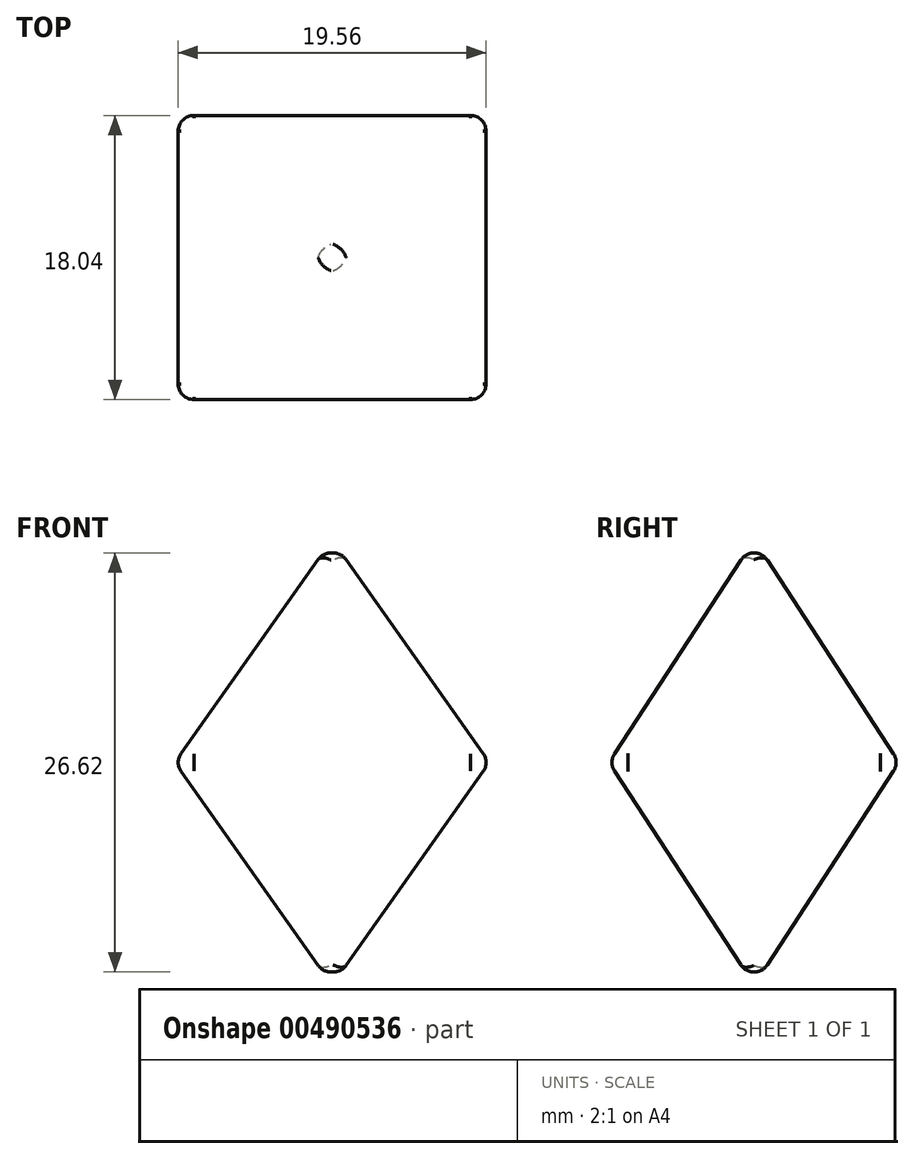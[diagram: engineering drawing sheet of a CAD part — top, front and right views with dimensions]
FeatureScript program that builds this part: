
annotation { "Feature Type Name" : "Feature", "Feature Type Description" : "" }
export const myFeature = defineFeature(function(context is Context, id is Id, definition is map)
    precondition{}
    {
        {
            var Q0;
            Q0=qCreatedBy(makeId("Top.planeOp"),FACE);
            var sketch = newSketch(context, id + "F0", { "sketchPlane" : qUnion([Q0])});
            skLineSegment(sketch, "E0.bottom", {"start": v(10, -9.22) * mm, "end": v(-10, -9.22) * mm});
            skLineSegment(sketch, "E0.top", {"start": v(10, 9.22) * mm, "end": v(-10, 9.22) * mm});
            skLineSegment(sketch, "E0.left", {"start": v(10, -9.22) * mm, "end": v(10, 9.22) * mm});
            skLineSegment(sketch, "E0.right", {"start": v(-10, -9.22) * mm, "end": v(-10, 9.22) * mm});
            skPoint(sketch, "E0.middle", {"position": v(0, 0) * mm});
            skPoint(sketch, "E1", {"position": v(-10, -9.22) * mm});
            skPoint(sketch, "E2", {"position": v(10, -9.22) * mm});
            skPoint(sketch, "E3", {"position": v(-10, 9.22) * mm});
            skPoint(sketch, "E4", {"position": v(10, 8.54) * mm});
            skSolve(sketch);
        }
        {
            var Q0;
            Q0=qCreatedBy(makeId("Front.planeOp"),FACE);
            var sketch = newSketch(context, id + "F1", { "sketchPlane" : qUnion([Q0])});
            skLineSegment(sketch, "E5", {"start": v(0, 0) * mm, "end": v(0, 14.14) * mm});
            skPoint(sketch, "E6", {"position": v(0, 14.14) * mm});
            skLineSegment(sketch, "E7.MirrorCS", {"start": v(0, 0) * mm, "end": v(0, -14.14) * mm});
            skSolve(sketch);
        }
        {
            var Q0;
            Q0=makeQuery(id+"F0.imprint","IMPRINT",FACE,{"disambiguationData":[TD([[makeQuery(id+"F0.imprint","IMPRINT",EDGE,{"derivedFrom":sQuery(id+"F0.wireOp",EDGE,"E0.bottom")}),-1.0]])]});
            var Q1;
            Q1=sQuery(id+"F1.wireOp",VERTEX,"E6");
            loft(context, id + "F2", {"sheetProfilesArray" : [{ "sheetProfileEntities" : qUnion([Q0]) }, { "sheetProfileEntities" : qUnion([Q1]) }]});
        }
        {
            var Q1;
            Q1=makeQuery(id+"F2.opLoft","CAP_FACE",FACE,{"disambiguationData":[OSD([makeQuery(id+"F0.imprint","IMPRINT",FACE,{"disambiguationData":[TD([[makeQuery(id+"F0.imprint","IMPRINT",EDGE,{"derivedFrom":sQuery(id+"F0.wireOp",EDGE,"E0.bottom")}),-1.0]])]})])],"isStart":true});
            var Q2;
            Q2=sQuery(id+"F1.wireOp",VERTEX,"E7.MirrorCS.end");
            loft(context, id + "F3", {"operationType" : NewBodyOperationType.ADD, "sheetProfilesArray" : [{ "sheetProfileEntities" : qUnion([Q1]) }, { "sheetProfileEntities" : qUnion([Q2]) }]});
        }
        {
            var Q0;
            Q0=makeQuery(id+"F3.opLoft","SWEPT_FACE",FACE,{"disambiguationData":[OSD([sQuery(id+"F0.wireOp",EDGE,"E0.bottom"),sQuery(id+"F0.wireOp",EDGE,"E0.top"),sQuery(id+"F0.wireOp",EDGE,"E0.left")])]});
            var Q1;
            Q1=makeQuery(id+"F2.opLoft","SWEPT_FACE",FACE,{"disambiguationData":[OSD([sQuery(id+"F0.wireOp",EDGE,"E0.top"),sQuery(id+"F0.wireOp",EDGE,"E0.left"),sQuery(id+"F0.wireOp",EDGE,"E0.right")])]});
            var Q2;
            Q2=makeQuery(id+"F3.opLoft","SWEPT_FACE",FACE,{"disambiguationData":[OSD([sQuery(id+"F0.wireOp",EDGE,"E0.bottom"),sQuery(id+"F0.wireOp",EDGE,"E0.top"),sQuery(id+"F0.wireOp",EDGE,"E0.right")])]});
            var Q3;
            Q3=makeQuery(id+"F2.opLoft","SWEPT_FACE",FACE,{"disambiguationData":[OSD([sQuery(id+"F0.wireOp",EDGE,"E0.bottom"),sQuery(id+"F0.wireOp",EDGE,"E0.left"),sQuery(id+"F0.wireOp",EDGE,"E0.right")])]});
            fillet(context, id + "F4", {"entities" : qUnion([Q0, Q1, Q2, Q3]), "radius" : 1 * mm, "tangentPropagation" : true, "allowEdgeOverflow" : false});
        }
    });
